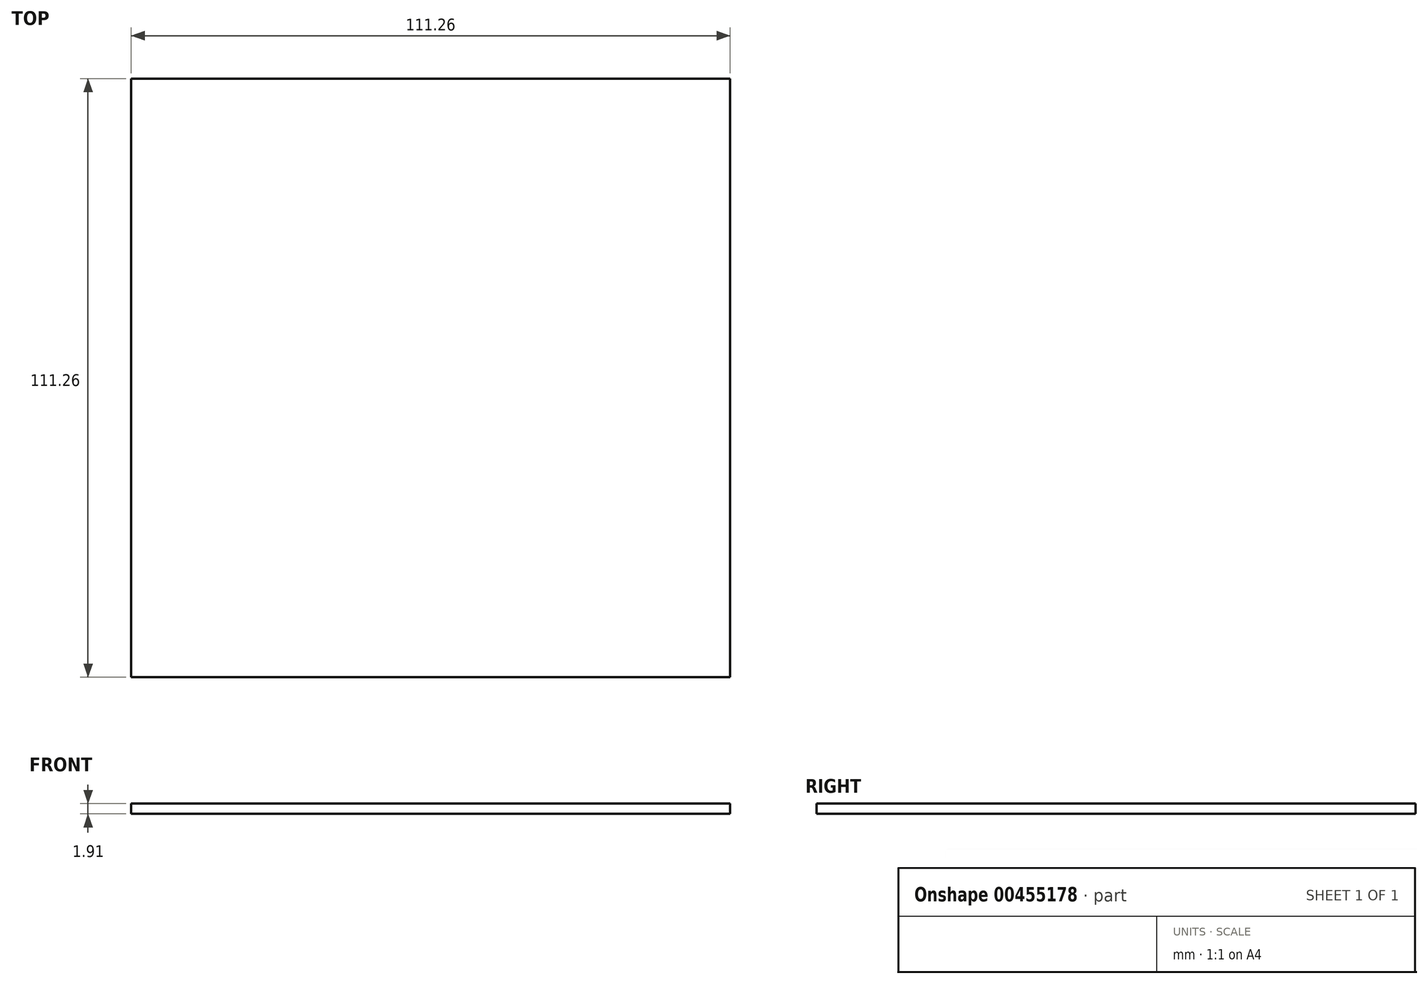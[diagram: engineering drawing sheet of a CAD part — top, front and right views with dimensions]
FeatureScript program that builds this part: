
annotation { "Feature Type Name" : "Feature", "Feature Type Description" : "" }
export const myFeature = defineFeature(function(context is Context, id is Id, definition is map)
    precondition{}
    {
        {
            var Q0;
            Q0=qCreatedBy(makeId("Top.planeOp"),FACE);
            var sketch = newSketch(context, id + "F0", { "sketchPlane" : qUnion([Q0])});
            skLineSegment(sketch, "E0.bottom", {"start": v(55.63, 55.63) * mm, "end": v(-55.63, 55.63) * mm});
            skLineSegment(sketch, "E0.top", {"start": v(55.63, -55.63) * mm, "end": v(-55.63, -55.63) * mm});
            skLineSegment(sketch, "E0.left", {"start": v(55.63, 55.63) * mm, "end": v(55.63, -55.63) * mm});
            skLineSegment(sketch, "E0.right", {"start": v(-55.63, 55.63) * mm, "end": v(-55.63, -55.63) * mm});
            skPoint(sketch, "E0.middle", {"position": v(0, 0) * mm});
            skSolve(sketch);
        }
        {
            var Q0;
            Q0=makeQuery(id+"F0.imprint","IMPRINT",FACE,{"disambiguationData":[TD([[makeQuery(id+"F0.imprint","IMPRINT",EDGE,{"derivedFrom":sQuery(id+"F0.wireOp",EDGE,"E0.bottom")}),1.0]])]});
            extrude(context, id + "F1", {"entities" : qUnion([Q0]), "depth" : 1.9 * mm});
        }
    });
